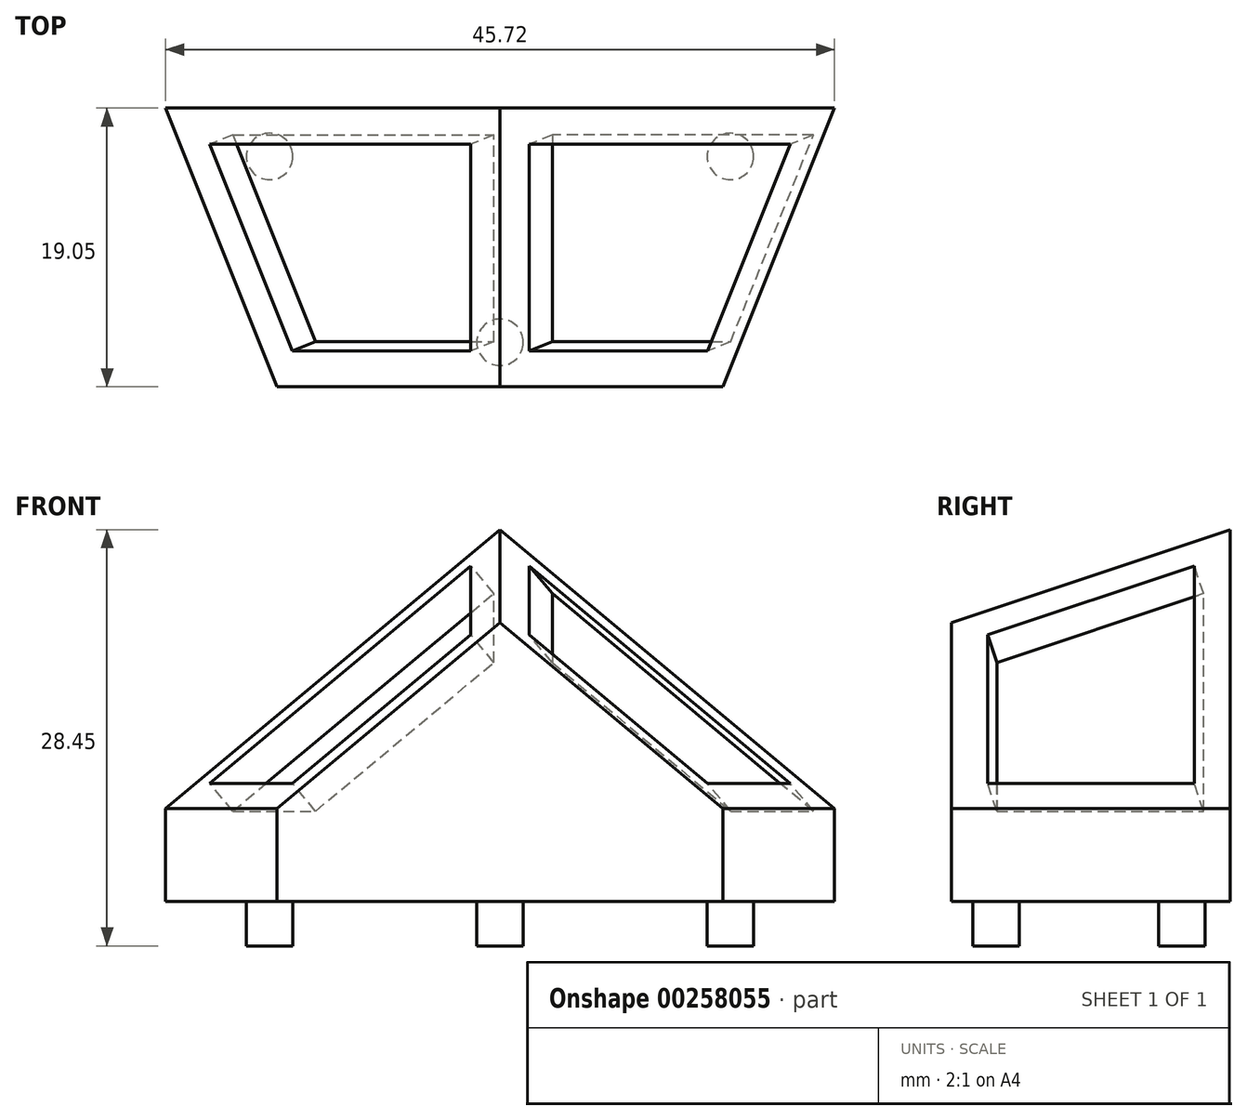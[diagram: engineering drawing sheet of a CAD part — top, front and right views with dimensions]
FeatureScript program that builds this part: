
annotation { "Feature Type Name" : "Feature", "Feature Type Description" : "" }
export const myFeature = defineFeature(function(context is Context, id is Id, definition is map)
    precondition{}
    {
        {
            var Q0;
            Q0=qCreatedBy(makeId("Front.planeOp"),FACE);
            var sketch = newSketch(context, id + "F0", { "sketchPlane" : qUnion([Q0])});
            skLineSegment(sketch, "E0", {"start": v(0, 25.4) * mm, "end": v(22.86, 6.35) * mm});
            skLineSegment(sketch, "E1", {"start": v(22.86, 6.35) * mm, "end": v(22.86, 0) * mm});
            skLineSegment(sketch, "E2", {"start": v(22.86, 0) * mm, "end": v(0, 0) * mm});
            skLineSegment(sketch, "E3.MirrorCS", {"start": v(0, 25.4) * mm, "end": v(-22.86, 6.35) * mm});
            skLineSegment(sketch, "E4.MirrorCS", {"start": v(-22.86, 6.35) * mm, "end": v(-22.86, 0) * mm});
            skLineSegment(sketch, "E5.MirrorCS", {"start": v(-22.86, 0) * mm, "end": v(0, 0) * mm});
            skSolve(sketch);
        }
        {
            var Q0;
            Q0=makeQuery(id+"F0.imprint","IMPRINT",FACE,{"disambiguationData":[TD([[makeQuery(id+"F0.imprint","IMPRINT",EDGE,{"derivedFrom":sQuery(id+"F0.wireOp",EDGE,"E0")}),-1.0]])]});
            cPlane(context, id + "F1", {"entities" : qUnion([Q0]), "cplaneType" : CPlaneType.OFFSET, "offset" : 19.05 * mm, "width" : 152.4 * mm, "height" : 152.4 * mm});
        }
        {
            var Q0;
            Q0=qCreatedBy(id+"F1.planeOp",FACE);
            var sketch = newSketch(context, id + "F2", { "sketchPlane" : qUnion([Q0])});
            skLineSegment(sketch, "E6", {"start": v(0, 0) * mm, "end": v(15.24, 0) * mm});
            skLineSegment(sketch, "E7", {"start": v(15.24, 0) * mm, "end": v(15.24, 6.35) * mm});
            skLineSegment(sketch, "E8", {"start": v(15.24, 6.35) * mm, "end": v(0, 19.05) * mm});
            skLineSegment(sketch, "E9.MirrorCS", {"start": v(-15.24, 6.35) * mm, "end": v(0, 19.05) * mm});
            skLineSegment(sketch, "E10.MirrorCS", {"start": v(-15.24, 0) * mm, "end": v(-15.24, 6.35) * mm});
            skLineSegment(sketch, "E11.MirrorCS", {"start": v(0, 0) * mm, "end": v(-15.24, 0) * mm});
            skSolve(sketch);
        }
        {
            var Q0;
            Q0=makeQuery(id+"F2.imprint","IMPRINT",FACE,{"disambiguationData":[TD([[makeQuery(id+"F2.imprint","IMPRINT",EDGE,{"derivedFrom":sQuery(id+"F2.wireOp",EDGE,"E6")}),1.0]])]});
            var Q1;
            Q1=makeQuery(id+"F0.imprint","IMPRINT",FACE,{"disambiguationData":[TD([[makeQuery(id+"F0.imprint","IMPRINT",EDGE,{"derivedFrom":sQuery(id+"F0.wireOp",EDGE,"E0")}),-1.0]])]});
            loft(context, id + "F3", {"sheetProfilesArray" : [{ "sheetProfileEntities" : qUnion([Q0]) }, { "sheetProfileEntities" : qUnion([Q1]) }]});
        }
        {
            var Q0;
            Q0=makeQuery(id+"F3.opLoft","SWEPT_FACE",FACE,{"disambiguationData":[OSD([sQuery(id+"F0.wireOp",EDGE,"E0"),sQuery(id+"F0.wireOp",EDGE,"E3.MirrorCS"),sQuery(id+"F0.wireOp",EDGE,"E4.MirrorCS"),sQuery(id+"F2.wireOp",EDGE,"E8"),sQuery(id+"F2.wireOp",EDGE,"E9.MirrorCS"),sQuery(id+"F2.wireOp",EDGE,"E10.MirrorCS")])]});
            var sketch = newSketch(context, id + "F4", { "sketchPlane" : qUnion([Q0])});
            skLineSegment(sketch, "E12.0", {"start": v(12.4, -9.98) * mm, "end": v(12.4, 4.91) * mm});
            skLineSegment(sketch, "E12.1", {"start": v(-3.14, -13.2) * mm, "end": v(12.4, -9.98) * mm});
            skLineSegment(sketch, "E12.2", {"start": v(-10.35, 0.21) * mm, "end": v(-3.14, -13.2) * mm});
            skLineSegment(sketch, "E12.3", {"start": v(-10.35, 0.21) * mm, "end": v(12.4, 4.91) * mm});
            skSolve(sketch);
        }
        {
            var Q0;
            Q0=makeQuery(id+"F3.opLoft","SWEPT_FACE",FACE,{"disambiguationData":[OSD([sQuery(id+"F0.wireOp",EDGE,"E0"),sQuery(id+"F0.wireOp",EDGE,"E1"),sQuery(id+"F0.wireOp",EDGE,"E3.MirrorCS"),sQuery(id+"F2.wireOp",EDGE,"E7"),sQuery(id+"F2.wireOp",EDGE,"E8"),sQuery(id+"F2.wireOp",EDGE,"E9.MirrorCS")])]});
            var sketch = newSketch(context, id + "F5", { "sketchPlane" : qUnion([Q0])});
            skLineSegment(sketch, "E13.0", {"start": v(3.14, -13.2) * mm, "end": v(10.35, 0.21) * mm});
            skLineSegment(sketch, "E13.1", {"start": v(-12.4, -9.98) * mm, "end": v(3.14, -13.2) * mm});
            skLineSegment(sketch, "E13.2", {"start": v(-12.4, 4.91) * mm, "end": v(-12.4, -9.98) * mm});
            skLineSegment(sketch, "E13.3", {"start": v(10.35, 0.21) * mm, "end": v(-12.4, 4.91) * mm});
            skSolve(sketch);
        }
        {
            var Q0;
            Q0=makeQuery(id+"F4.imprint","IMPRINT",FACE,{"disambiguationData":[TD([[makeQuery(id+"F4.imprint","IMPRINT",EDGE,{"derivedFrom":sQuery(id+"F4.wireOp",EDGE,"E12.0")}),1.0]])]});
            var Q1;
            Q1=makeQuery(id+"F5.imprint","IMPRINT",FACE,{"disambiguationData":[TD([[makeQuery(id+"F5.imprint","IMPRINT",EDGE,{"derivedFrom":sQuery(id+"F5.wireOp",EDGE,"E13.0")}),1.0]])]});
            extrude(context, id + "F6", {"entities" : qUnion([Q0, Q1]), "operationType" : NewBodyOperationType.REMOVE, "oppositeDirection" : true, "depth" : 2.54 * mm});
        }
        {
            var Q0;
            Q0=makeQuery(id+"F3.opLoft","SWEPT_FACE",FACE,{"disambiguationData":[OSD([sQuery(id+"F0.wireOp",EDGE,"E1"),sQuery(id+"F0.wireOp",EDGE,"E2"),sQuery(id+"F0.wireOp",EDGE,"E5.MirrorCS"),sQuery(id+"F2.wireOp",EDGE,"E6"),sQuery(id+"F2.wireOp",EDGE,"E7"),sQuery(id+"F2.wireOp",EDGE,"E11.MirrorCS")])]});
            var sketch = newSketch(context, id + "F7", { "sketchPlane" : qUnion([Q0])});
            skCircle(sketch, "E14", {"center": v(0, 16) * mm, "radius": 1.59 * mm});
            skCircle(sketch, "E15", {"center": v(15.75, 3.3) * mm, "radius": 1.59 * mm});
            skCircle(sketch, "E16", {"center": v(-15.75, 3.3) * mm, "radius": 1.59 * mm});
            skSolve(sketch);
        }
        {
            var Q0;
            Q0=makeQuery(id+"F7.imprint","IMPRINT",FACE,{"disambiguationData":[TD([[makeQuery(id+"F7.imprint","IMPRINT",EDGE,{"derivedFrom":sQuery(id+"F7.wireOp",EDGE,"E14")}),1.0]])]});
            var Q1;
            Q1=makeQuery(id+"F7.imprint","IMPRINT",FACE,{"disambiguationData":[TD([[makeQuery(id+"F7.imprint","IMPRINT",EDGE,{"derivedFrom":sQuery(id+"F7.wireOp",EDGE,"E15")}),1.0]])]});
            var Q2;
            Q2=makeQuery(id+"F7.imprint","IMPRINT",FACE,{"disambiguationData":[TD([[makeQuery(id+"F7.imprint","IMPRINT",EDGE,{"derivedFrom":sQuery(id+"F7.wireOp",EDGE,"E16")}),1.0]])]});
            extrude(context, id + "F8", {"entities" : qUnion([Q0, Q1, Q2]), "operationType" : NewBodyOperationType.ADD, "depth" : 3.05 * mm});
        }
    });
